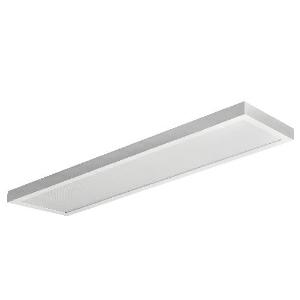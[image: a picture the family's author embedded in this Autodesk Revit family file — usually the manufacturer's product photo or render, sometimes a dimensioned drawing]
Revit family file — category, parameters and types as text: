
# Revit family: ledpanels-sf-p_l12-40w-ble2-830_840_542003156100_7715
name_source: partatom
category: Lighting Fixtures
units: mm (PartAtom-declared; Revit-internal decimal feet)

## family parameters
Cut with Voids When Loaded = No
Host = Face
Light Source = No
Part Type = Normal
Room Calculation Point = No
Round Connector Dimension = Use Diameter
Shared = No

## types (1)
- LEDPanelS-Sf-P L12-40W-BLE2-830/840 (1 x LED, 5000 lm, 4000)
    Apparent Load = 40 VA
    Approval mark = CE, ENEC
    CIE Flux Codes = 60 87 97 100 100
    Color Rendering = 80
    Color Temperature = 4000
    Control Gear = Electronic ballast
    Default Elevation = 1800 mm
    Description = Panel Performer Surface Mounted 1274x370mm-40W-5000lm-3/4000K-Bluetooth
    Frequency = 60 Hz
    Height = 55 mm
    Lamp = 1 x LED
    Lamp Light Flux = 5000 lm
    Lamp count = 1
    Length = 1274 mm
    Luminous efficacy = 125 lm/W
    Manufacturer = OPPLE
    ModVariant = No
    Model = 542003156100
    Mounting Place = Ceiling
    Mounting Type = Surface mounted
    Number of Poles = 1
    OnlyDefault = Yes
    Power Factor = 1
    Product Name = LEDPanelS-Sf-P L12-40W-BLE2-830/840
    Product group = Ceiling mounted luminaire
    ProductGroupID = 3
    Protection Class = Safety extra-low voltage
    Protection Degree = IP 20
    RLX_Detail_Level = 1
    RLX_Emergency_Light_Flux = 0 lm
    RLX_Emergency_Type = 0
    RLX_Emergency_Type_DB = No
    RlxData = <blob elided: 96085 chars, md5=36c6c2c9>
    Socket = socket
    Standby Power = 0 W
    System Light Flux = 5000 lm
    System Power = 40 W
    Type Comments = Product without accessories
    Type Image = web_surface_pl.jpg
    URL = http://relux.com
    VarID = ---
    Voltage = 230 V
    Voltage Range = 220-240 V
    Weight = 0.00 kg
    Width = 370 mm

## geometry (parser evidence)
native form markers: Blend x4, Sweep x10
no freeform markers — native parametric forms only
